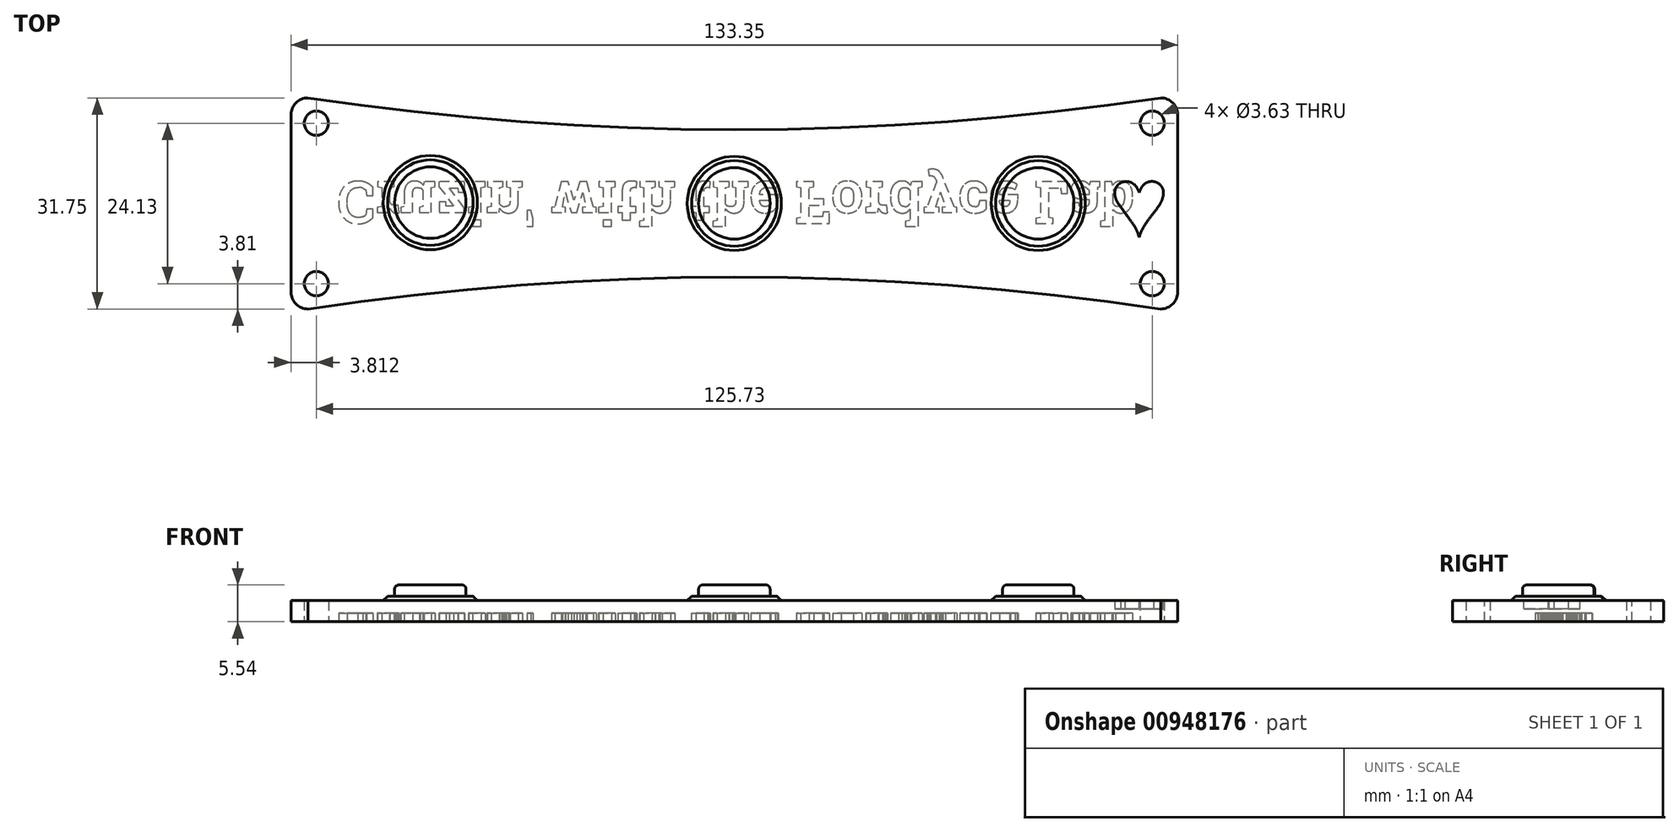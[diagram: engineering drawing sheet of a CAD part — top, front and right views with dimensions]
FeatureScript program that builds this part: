
annotation { "Feature Type Name" : "Feature", "Feature Type Description" : "" }
export const myFeature = defineFeature(function(context is Context, id is Id, definition is map)
    precondition{}
    {
        {
            var Q0;
            Q0=qCreatedBy(makeId("Top.planeOp"),FACE);
            var sketch = newSketch(context, id + "F0", { "sketchPlane" : qUnion([Q0])});
            skLineSegment(sketch, "E0.bottom", {"start": v(51.88, 0) * mm, "end": v(-81.47, 0) * mm});
            skLineSegment(sketch, "E0.top", {"start": v(51.88, -31.75) * mm, "end": v(-81.47, -31.75) * mm});
            skLineSegment(sketch, "E0.left", {"start": v(51.88, 0) * mm, "end": v(51.88, -31.75) * mm});
            skLineSegment(sketch, "E0.right", {"start": v(-81.47, 0) * mm, "end": v(-81.47, -31.75) * mm});
            skCircle(sketch, "E1", {"center": v(-77.66, -27.94) * mm, "radius": 1.82 * mm});
            skLineSegment(sketch, "E2", {"start": v(-81.47, -15.88) * mm, "end": v(51.88, -15.88) * mm, "construction": true});
            skLineSegment(sketch, "E3", {"start": v(-14.8, -31.75) * mm, "end": v(-14.8, 0) * mm, "construction": true});
            skCircle(sketch, "E4.MirrorC", {"center": v(-77.66, -3.81) * mm, "radius": 1.82 * mm});
            skCircle(sketch, "E5.MirrorC", {"center": v(48.07, -27.94) * mm, "radius": 1.82 * mm});
            skCircle(sketch, "E6.MirrorC", {"center": v(48.07, -3.8) * mm, "radius": 1.82 * mm});
            skLineSegment(sketch, "E7.left", {"start": v(-81.47, -8.22) * mm, "end": v(-81.47, -24.11) * mm});
            skLineSegment(sketch, "E7.right", {"start": v(51.88, -8.22) * mm, "end": v(51.88, -24.11) * mm});
            skSolve(sketch);
        }
        {
            var Q0;
            Q0=makeQuery(id+"F0.imprint","IMPRINT",FACE,{"disambiguationData":[TD([[makeQuery(id+"F0.imprint","IMPRINT",EDGE,{"derivedFrom":sQuery(id+"F0.wireOp",EDGE,"E0.bottom")}),1.0]])]});
            extrude(context, id + "F1", {"entities" : qUnion([Q0]), "flatOperationType" : FlatOperationType.REMOVE, "depth" : 3.17 * mm, "offsetDistance" : 25.4 * mm, "domain" : OperationDomain.MODEL});
        }
        {
            var Q0;
            Q0=makeQuery(id+"F1.opExtrude","SWEPT_EDGE",EDGE,{"disambiguationData":[OSD([sQuery(id+"F0.wireOp",EDGE,"E0.bottom"),sQuery(id+"F0.wireOp",EDGE,"E0.right")])]});
            var Q1;
            Q1=makeQuery(id+"F1.opExtrude","SWEPT_EDGE",EDGE,{"disambiguationData":[OSD([sQuery(id+"F0.wireOp",EDGE,"E0.top"),sQuery(id+"F0.wireOp",EDGE,"E0.right")])]});
            var Q2;
            Q2=makeQuery(id+"F1.opExtrude","SWEPT_EDGE",EDGE,{"disambiguationData":[OSD([sQuery(id+"F0.wireOp",EDGE,"E0.bottom"),sQuery(id+"F0.wireOp",EDGE,"E0.left")])]});
            var Q3;
            Q3=makeQuery(id+"F1.opExtrude","SWEPT_EDGE",EDGE,{"disambiguationData":[OSD([sQuery(id+"F0.wireOp",EDGE,"E0.top"),sQuery(id+"F0.wireOp",EDGE,"E0.left")])]});
            fillet(context, id + "F2", {"entities" : qUnion([Q0, Q1, Q2, Q3]), "radius" : 2.54 * mm, "tangentPropagation" : true, "allowEdgeOverflow" : false});
        }
        {
            var Q0;
            Q0=makeQuery(id+"F1.opExtrude","CAP_FACE",FACE,{"disambiguationData":[OSD([sQuery(id+"F0.wireOp",EDGE,"E0.bottom"),sQuery(id+"F0.wireOp",EDGE,"E0.top"),sQuery(id+"F0.wireOp",EDGE,"E0.left"),sQuery(id+"F0.wireOp",EDGE,"E0.right"),sQuery(id+"F0.wireOp",EDGE,"E1"),sQuery(id+"F0.wireOp",EDGE,"E4.MirrorC"),sQuery(id+"F0.wireOp",EDGE,"E5.MirrorC"),sQuery(id+"F0.wireOp",EDGE,"E6.MirrorC"),sQuery(id+"F0.wireOp",EDGE,"E7.left"),sQuery(id+"F0.wireOp",EDGE,"E7.right")])],"isStart":false});
            var sketch = newSketch(context, id + "F3", { "sketchPlane" : qUnion([Q0])});
            skLineSegment(sketch, "E8", {"start": v(-81.47, -15.88) * mm, "end": v(51.88, -15.88) * mm, "construction": true});
            skLineSegment(sketch, "E9", {"start": v(-14.8, 0) * mm, "end": v(-14.8, -31.75) * mm});
            skCircle(sketch, "E10", {"center": v(-14.8, -15.88) * mm, "radius": 5.37 * mm});
            skLineSegment(sketch, "E11", {"start": v(-40.18, -15.88) * mm, "end": v(102.03, -15.87) * mm, "construction": true});
            skLineSegment(sketch, "E12", {"start": v(26.5, 0) * mm, "end": v(26.5, -31.75) * mm});
            skCircle(sketch, "E13", {"center": v(30.93, -15.88) * mm, "radius": 5.37 * mm});
            skLineSegment(sketch, "E14", {"start": v(-127.19, -15.76) * mm, "end": v(6.16, -15.76) * mm, "construction": true});
            skLineSegment(sketch, "E15", {"start": v(-57.94, 0.12) * mm, "end": v(-57.94, -31.63) * mm});
            skCircle(sketch, "E16", {"center": v(-60.51, -15.76) * mm, "radius": 5.37 * mm});
            skCircle(sketch, "E17", {"center": v(-60.51, -15.76) * mm, "radius": 8.97 * mm});
            skCircle(sketch, "E18", {"center": v(-14.8, -15.88) * mm, "radius": 8.97 * mm});
            skCircle(sketch, "E19", {"center": v(30.93, -15.88) * mm, "radius": 8.97 * mm});
            skSolve(sketch);
        }
        {
            var Q0;
            {var subQ0=sQuery(id+"F3.wireOp",EDGE,"E17");var subQ1=sQuery(id+"F3.wireOp",EDGE,"E15");var subQ2=makeQuery(id+"F3.imprint","INTERSECT",VERTEX,{"disambiguationData":[OD(0.0)],"derivedFrom":[subQ1,subQ0]});Q0=makeQuery(id+"F3.imprint","IMPRINT",FACE,{"disambiguationData":[TD([[makeQuery(id+"F3.imprint","IMPRINT",EDGE,{"disambiguationData":[TD([[subQ2,-1.0]])],"derivedFrom":subQ1}),-1.0]])]});}
            var Q1;
            {var subQ0=sQuery(id+"F3.wireOp",EDGE,"E17");var subQ1=sQuery(id+"F3.wireOp",EDGE,"E15");var subQ2=makeQuery(id+"F3.imprint","INTERSECT",VERTEX,{"disambiguationData":[OD(0.0)],"derivedFrom":[subQ1,subQ0]});Q1=makeQuery(id+"F3.imprint","IMPRINT",FACE,{"disambiguationData":[TD([[makeQuery(id+"F3.imprint","IMPRINT",EDGE,{"disambiguationData":[TD([[subQ2,-1.0]])],"derivedFrom":subQ1}),1.0]])]});}
            var Q2;
            {var subQ0=sQuery(id+"F3.wireOp",EDGE,"E18");var subQ1=sQuery(id+"F3.wireOp",EDGE,"E9");var subQ2=makeQuery(id+"F3.imprint","INTERSECT",VERTEX,{"disambiguationData":[OD(0.0)],"derivedFrom":[subQ1,subQ0]});Q2=makeQuery(id+"F3.imprint","IMPRINT",FACE,{"disambiguationData":[TD([[makeQuery(id+"F3.imprint","IMPRINT",EDGE,{"disambiguationData":[TD([[subQ2,-1.0]])],"derivedFrom":subQ1}),-1.0]])]});}
            var Q3;
            {var subQ0=sQuery(id+"F3.wireOp",EDGE,"E18");var subQ1=sQuery(id+"F3.wireOp",EDGE,"E9");var subQ2=makeQuery(id+"F3.imprint","INTERSECT",VERTEX,{"disambiguationData":[OD(0.0)],"derivedFrom":[subQ1,subQ0]});Q3=makeQuery(id+"F3.imprint","IMPRINT",FACE,{"disambiguationData":[TD([[makeQuery(id+"F3.imprint","IMPRINT",EDGE,{"disambiguationData":[TD([[subQ2,-1.0]])],"derivedFrom":subQ1}),1.0]])]});}
            var Q4;
            {var subQ0=sQuery(id+"F3.wireOp",EDGE,"E19");var subQ1=sQuery(id+"F3.wireOp",EDGE,"E12");var subQ2=makeQuery(id+"F3.imprint","INTERSECT",VERTEX,{"disambiguationData":[OD(0.0)],"derivedFrom":[subQ1,subQ0]});Q4=makeQuery(id+"F3.imprint","IMPRINT",FACE,{"disambiguationData":[TD([[makeQuery(id+"F3.imprint","IMPRINT",EDGE,{"disambiguationData":[TD([[subQ2,-1.0]])],"derivedFrom":subQ1}),-1.0]])]});}
            var Q5;
            {var subQ0=sQuery(id+"F3.wireOp",EDGE,"E19");var subQ1=sQuery(id+"F3.wireOp",EDGE,"E12");var subQ2=makeQuery(id+"F3.imprint","INTERSECT",VERTEX,{"disambiguationData":[OD(0.0)],"derivedFrom":[subQ1,subQ0]});Q5=makeQuery(id+"F3.imprint","IMPRINT",FACE,{"disambiguationData":[TD([[makeQuery(id+"F3.imprint","IMPRINT",EDGE,{"disambiguationData":[TD([[subQ2,-1.0]])],"derivedFrom":subQ1}),1.0]])]});}
            extrude(context, id + "F4", {"entities" : qUnion([Q0, Q1, Q2, Q3, Q4, Q5]), "operationType" : NewBodyOperationType.ADD, "depth" : (.125 + (.85 - .32)) * mm, "offsetDistance" : 25.4 * mm});
        }
        {
            var Q0;
            Q0=makeQuery(id+"F4.boolean.opBoolean","SPLIT",FACE,{"disambiguationData":[TD([makeQuery(id+"F4.opExtrude","SWEPT_FACE",FACE,{"disambiguationData":[OSD([sQuery(id+"F3.wireOp",EDGE,"E16")])]})])],"derivedFrom":makeQuery(id+"F1.opExtrude","CAP_FACE",FACE,{"disambiguationData":[OSD([sQuery(id+"F0.wireOp",EDGE,"E0.bottom"),sQuery(id+"F0.wireOp",EDGE,"E0.top"),sQuery(id+"F0.wireOp",EDGE,"E0.left"),sQuery(id+"F0.wireOp",EDGE,"E0.right"),sQuery(id+"F0.wireOp",EDGE,"E1"),sQuery(id+"F0.wireOp",EDGE,"E4.MirrorC"),sQuery(id+"F0.wireOp",EDGE,"E5.MirrorC"),sQuery(id+"F0.wireOp",EDGE,"E6.MirrorC"),sQuery(id+"F0.wireOp",EDGE,"E7.left"),sQuery(id+"F0.wireOp",EDGE,"E7.right")])],"isStart":false})});
            var Q1;
            Q1=makeQuery(id+"F4.boolean.opBoolean","SPLIT",FACE,{"disambiguationData":[TD([makeQuery(id+"F4.opExtrude","SWEPT_FACE",FACE,{"disambiguationData":[OSD([sQuery(id+"F3.wireOp",EDGE,"E10")])]})])],"derivedFrom":makeQuery(id+"F1.opExtrude","CAP_FACE",FACE,{"disambiguationData":[OSD([sQuery(id+"F0.wireOp",EDGE,"E0.bottom"),sQuery(id+"F0.wireOp",EDGE,"E0.top"),sQuery(id+"F0.wireOp",EDGE,"E0.left"),sQuery(id+"F0.wireOp",EDGE,"E0.right"),sQuery(id+"F0.wireOp",EDGE,"E1"),sQuery(id+"F0.wireOp",EDGE,"E4.MirrorC"),sQuery(id+"F0.wireOp",EDGE,"E5.MirrorC"),sQuery(id+"F0.wireOp",EDGE,"E6.MirrorC"),sQuery(id+"F0.wireOp",EDGE,"E7.left"),sQuery(id+"F0.wireOp",EDGE,"E7.right")])],"isStart":false})});
            var Q2;
            Q2=makeQuery(id+"F4.boolean.opBoolean","SPLIT",FACE,{"disambiguationData":[TD([makeQuery(id+"F4.opExtrude","SWEPT_FACE",FACE,{"disambiguationData":[OSD([sQuery(id+"F3.wireOp",EDGE,"E13")])]})])],"derivedFrom":makeQuery(id+"F1.opExtrude","CAP_FACE",FACE,{"disambiguationData":[OSD([sQuery(id+"F0.wireOp",EDGE,"E0.bottom"),sQuery(id+"F0.wireOp",EDGE,"E0.top"),sQuery(id+"F0.wireOp",EDGE,"E0.left"),sQuery(id+"F0.wireOp",EDGE,"E0.right"),sQuery(id+"F0.wireOp",EDGE,"E1"),sQuery(id+"F0.wireOp",EDGE,"E4.MirrorC"),sQuery(id+"F0.wireOp",EDGE,"E5.MirrorC"),sQuery(id+"F0.wireOp",EDGE,"E6.MirrorC"),sQuery(id+"F0.wireOp",EDGE,"E7.left"),sQuery(id+"F0.wireOp",EDGE,"E7.right")])],"isStart":false})});
            extrude(context, id + "F5", {"entities" : qUnion([Q0, Q1, Q2]), "operationType" : NewBodyOperationType.ADD, "depth" : 2.36 * mm, "offsetDistance" : 25.4 * mm});
        }
        {
            var Q0;
            Q0=makeQuery(id+"F5.opExtrude","CAP_EDGE",EDGE,{"disambiguationData":[OSD([sQuery(id+"F3.wireOp",EDGE,"E16")])],"isStart":false});
            var Q1;
            Q1=makeQuery(id+"F5.opExtrude","CAP_EDGE",EDGE,{"disambiguationData":[OSD([sQuery(id+"F3.wireOp",EDGE,"E10")])],"isStart":false});
            var Q2;
            Q2=makeQuery(id+"F5.opExtrude","CAP_EDGE",EDGE,{"disambiguationData":[OSD([sQuery(id+"F3.wireOp",EDGE,"E13")])],"isStart":false});
            fillet(context, id + "F6", {"entities" : qUnion([Q0, Q1, Q2]), "radius" : 0.64 * mm, "tangentPropagation" : true, "allowEdgeOverflow" : false});
        }
        {
            var Q0;
            Q0=makeQuery(id+"F4.opExtrude","CAP_EDGE",EDGE,{"disambiguationData":[OSD([sQuery(id+"F3.wireOp",EDGE,"E17")])],"isStart":false});
            var Q1;
            Q1=makeQuery(id+"F4.opExtrude","CAP_EDGE",EDGE,{"disambiguationData":[OSD([sQuery(id+"F3.wireOp",EDGE,"E18")])],"isStart":false});
            var Q2;
            Q2=makeQuery(id+"F4.opExtrude","CAP_EDGE",EDGE,{"disambiguationData":[OSD([sQuery(id+"F3.wireOp",EDGE,"E19")])],"isStart":false});
            chamfer(context, id + "F7", {"entities" : qUnion([Q0, Q1, Q2]), "width" : 2.54 * mm, "tangentPropagation" : true});
        }
        {
            var Q0;
            {var subQ0=sQuery(id+"F0.wireOp",EDGE,"E6.MirrorC");var subQ1=sQuery(id+"F0.wireOp",EDGE,"E0.left");var subQ2=sQuery(id+"F0.wireOp",EDGE,"E0.bottom");var subQ3=sQuery(id+"F0.wireOp",EDGE,"E5.MirrorC");var subQ4=sQuery(id+"F0.wireOp",EDGE,"E4.MirrorC");var subQ5=sQuery(id+"F0.wireOp",EDGE,"E1");var subQ6=sQuery(id+"F0.wireOp",EDGE,"E0.right");var subQ7=sQuery(id+"F0.wireOp",EDGE,"E7.left");var subQ8=sQuery(id+"F0.wireOp",EDGE,"E0.top");var subQ9=sQuery(id+"F0.wireOp",EDGE,"E7.right");Q0=makeQuery(id+"F4.boolean.opBoolean","SPLIT",FACE,{"disambiguationData":[TD([makeQuery(id+"F1.opExtrude","SWEPT_FACE",FACE,{"disambiguationData":[OSD([subQ2])]})])],"derivedFrom":makeQuery(id+"F1.opExtrude","CAP_FACE",FACE,{"disambiguationData":[OSD([subQ2,subQ8,subQ1,subQ6,subQ5,subQ4,subQ3,subQ0,subQ7,subQ9])],"isStart":false})});}
            var sketch = newSketch(context, id + "F8", { "sketchPlane" : qUnion([Q0])});
            skArc(sketch, "E20", {"start": v(-78.93, 0) * mm, "mid": v(-14.8, -4.79) * mm, "end": v(49.34, 0) * mm});
            skArc(sketch, "E21", {"start": v(49.34, -31.75) * mm, "mid": v(-14.8, -26.96) * mm, "end": v(-78.93, -31.75) * mm});
            skSolve(sketch);
        }
        {
            var Q0;
            {var subQ0=sQuery(id+"F8.wireOp",EDGE,"E20");Q0=makeQuery(id+"F8.imprint","IMPRINT",FACE,{"disambiguationData":[TD([[makeQuery(id+"F8.imprint","IMPRINT",EDGE,{"derivedFrom":subQ0}),1.0]])]});}
            var Q1;
            {var subQ0=sQuery(id+"F8.wireOp",EDGE,"E21");Q1=makeQuery(id+"F8.imprint","IMPRINT",FACE,{"disambiguationData":[TD([[makeQuery(id+"F8.imprint","IMPRINT",EDGE,{"derivedFrom":subQ0}),1.0]])]});}
            extrude(context, id + "F9", {"entities" : qUnion([Q0, Q1]), "operationType" : NewBodyOperationType.REMOVE, "oppositeDirection" : true, "depth" : 3.17 * mm, "offsetDistance" : 25.4 * mm});
        }
        {
            var Q0;
            Q0=makeQuery(id+"F1.opExtrude","CAP_FACE",FACE,{"disambiguationData":[OSD([sQuery(id+"F0.wireOp",EDGE,"E0.bottom"),sQuery(id+"F0.wireOp",EDGE,"E0.top"),sQuery(id+"F0.wireOp",EDGE,"E0.left"),sQuery(id+"F0.wireOp",EDGE,"E0.right"),sQuery(id+"F0.wireOp",EDGE,"E1"),sQuery(id+"F0.wireOp",EDGE,"E4.MirrorC"),sQuery(id+"F0.wireOp",EDGE,"E5.MirrorC"),sQuery(id+"F0.wireOp",EDGE,"E6.MirrorC"),sQuery(id+"F0.wireOp",EDGE,"E7.left"),sQuery(id+"F0.wireOp",EDGE,"E7.right")])],"isStart":true});
            var sketch = newSketch(context, id + "F10", { "sketchPlane" : qUnion([Q0])});
            skLineSegment(sketch, "E22", {"start": v(-81.47, 15.88) * mm, "end": v(51.88, 15.88) * mm, "construction": true});
            skSolve(sketch);
        }
        {
            var Q0;
            {var subQ7=sQuery(id+"F0.wireOp",EDGE,"E1");Q0=makeQuery(id+"F10.imprint","IMPRINT",FACE,{"disambiguationData":[TD([[makeQuery(id+"F10.imprint","IMPRINT",EDGE,{"derivedFrom":makeQuery(id+"F1.opExtrude","CAP_EDGE",EDGE,{"disambiguationData":[OSD([subQ7])],"isStart":true})}),1.0]])]});}
            var sketch = newSketch(context, id + "F11", { "sketchPlane" : qUnion([Q0])});
            skText(sketch, "E23", { "text": "Cruzin\' with the Fordyce Lab", "fontName": "RobotoSlab-Bold.ttf"});
            const initialGuessF11  = {"E23": [-0.07452, 0.0126, 1, 0, 0.00635]};
            skSetInitialGuess(sketch, initialGuessF11);
            skSolve(sketch);
        }
        {
            var Q0;
            {var subQ0=sQuery(id+"F0.wireOp",EDGE,"E6.MirrorC");var subQ1=sQuery(id+"F0.wireOp",EDGE,"E0.left");var subQ2=sQuery(id+"F0.wireOp",EDGE,"E0.bottom");var subQ3=sQuery(id+"F0.wireOp",EDGE,"E5.MirrorC");var subQ4=sQuery(id+"F0.wireOp",EDGE,"E4.MirrorC");var subQ5=sQuery(id+"F0.wireOp",EDGE,"E1");var subQ6=sQuery(id+"F0.wireOp",EDGE,"E0.right");var subQ7=sQuery(id+"F0.wireOp",EDGE,"E7.left");var subQ8=sQuery(id+"F0.wireOp",EDGE,"E0.top");var subQ9=sQuery(id+"F0.wireOp",EDGE,"E7.right");Q0=makeQuery(id+"F4.boolean.opBoolean","SPLIT",FACE,{"disambiguationData":[TD([makeQuery(id+"F1.opExtrude","SWEPT_FACE",FACE,{"disambiguationData":[OSD([subQ2])]})])],"derivedFrom":makeQuery(id+"F1.opExtrude","CAP_FACE",FACE,{"disambiguationData":[OSD([subQ2,subQ8,subQ1,subQ6,subQ5,subQ4,subQ3,subQ0,subQ7,subQ9])],"isStart":false})});}
            var sketch = newSketch(context, id + "F12", { "sketchPlane" : qUnion([Q0])});
            skText(sketch, "E24", { "text": "♥", "fontName": "Tinos-Regular.ttf"});
            skPoint(sketch, "E25.startSnap0", {"position": v(41.69, -15.52) * mm});
            skLineSegment(sketch, "E26", {"start": v(39.9, -15.82) * mm, "end": v(51.88, -15.82) * mm, "construction": true});
            skPoint(sketch, "E27", {"position": v(45.89, -15.82) * mm});
            const initialGuessF12  = {"E24": [0.04169, -0.02085, 1, 0, 0.01067]};
            skSetInitialGuess(sketch, initialGuessF12);
            skSolve(sketch);
        }
        {
            var Q0;
            Q0 = qSketchRegion(id + "F12", true);
            extrude(context, id + "F13", {"entities" : qUnion([Q0]), "operationType" : NewBodyOperationType.REMOVE, "oppositeDirection" : true, "depth" : 1.27 * mm, "offsetDistance" : 25.4 * mm});
        }
        {
            var Q0;
            Q0 = qSketchRegion(id + "F11", true);
            extrude(context, id + "F14", {"entities" : qUnion([Q0]), "operationType" : NewBodyOperationType.REMOVE, "oppositeDirection" : true, "depth" : 1.27 * mm, "offsetDistance" : 25.4 * mm});
        }
    });
